# Revit family: BLAUBERG-KOMFORT_EC_S5B_270
name_source: partatom
category: Mechanical Equipment
units: mm (PartAtom-declared; Revit-internal decimal feet)

## family parameters
Always vertical = Yes
Classification = None
Cut with Voids When Loaded = No
OmniClass Number = 23.75.35.14
OmniClass Title = Air Handling Units
Part Type = Normal
Room Calculation Point = No
Round Connector Dimension = Use Diameter
Shared = No
Work Plane-Based = No

## types (4) — shared parameters
B = 300 mm
B1 = 91 mm  [stored 0.298556 ft]
B2 = 91 mm  [stored 0.298556 ft]
BHalf = 150 mm
Casing Material = Polypropylene Black
CasingR = 100 mm  [stored 0.328084 ft]
Current = 1 A
D = 125 mm  [stored 0.410105 ft]
Description = Air Handling Unit
DrainConB1 = 143 mm
DrainConB2 = 143 mm
Duct Connection Diameter = 125 mm  [stored 0.410105 ft]
ElConH = 520 mm  [stored 1.70604 ft]
ElConL = 289 mm  [stored 0.948163 ft]
Extract Air Filter = G4
Family Version = 1.0
FloorSupportH = 20 mm  [stored 0.0656168 ft]
FloorSupportHCalc = 30 mm  [stored 0.0984252 ft]
Front Maintenance Zone Height = 500 mm  [stored 1.64042 ft]
H = 844 mm  [stored 2.76903 ft]
HDuctCon = 50 mm  [stored 0.164042 ft]
Heat Exchanger Type = counter-flow
L = 578 mm  [stored 1.89633 ft]
L1 = 96 mm  [stored 0.314961 ft]
L2 = 225 mm  [stored 0.738189 ft]
L3 = 96 mm  [stored 0.314961 ft]
L4 = 225 mm  [stored 0.738189 ft]
Load Classification = HVAC
Maintenance Zone Material = Maintenance Zone
Manufacturer = Blauberg
Maximum Air Flow = 300 m³/h
Maximum Unit Power = 162 W
Metal Material = Metal Zinc
Number of Poles = 1
Plastic Material = Polypropylene Black
Power = 162 W
Power Factor = 1
RPM (min-1) = 3200
ServiceDoorH = 424 mm  [stored 1.39108 ft]
ServiceDoorH1 = 10 mm  [stored 0.0328084 ft]
ServiceDoorL = 436 mm  [stored 1.43045 ft]
ServiceDoorR = 55 mm  [stored 0.180446 ft]
ServiceDoorThickness = 5 mm  [stored 0.0164042 ft]
Sevice Door Material = Polypropylene Blue
Sound Pressure Level at 3 m (dBA) = 34
Supply Air Filter = G4 (option F8)
Transported Air Temperature (°C) = -25…+40
URL = https://blaubergventilatoren.de
Unit Current = 1 A
Voltage = 230 V
dBFloorSupports = 55 mm  [stored 0.180446 ft]
dLFloorSupports = 80 mm  [stored 0.262467 ft]

## per-type parameters (varying)
| type | Drain Connection Diameter | DrainPipe | DrainPipeD | Heat Exchanger Material | Heat recovery efficiency (%) | SEC Class | Type Comments | Weight |
| KOMFORT EC S5B 270 S21 | 15 mm  [stored 0.0492126 ft] | Yes | 15 mm  [stored 0.0492126 ft] | polystyrene | 87..98 | A+ | Air Handling Unit KOMFORT EC S5B 270 S21 | 13.00 kg |
| KOMFORT EC S5B 270-E S21 | 0 mm  [stored 0 ft] | No | 1 mm  [stored 0.00328084 ft] | enthalpy | 72..94 | A | Air Handling Unit KOMFORT EC S5B 270-E S21 | 13.50 kg |
| KOMFORT EC S5B 270 S14 | 15 mm  [stored 0.0492126 ft] | Yes | 15 mm  [stored 0.0492126 ft] | polystyrene | 87..98 | A+ | Air Handling Unit KOMFORT EC S5B 270 S14 | 13.00 kg |
| KOMFORT EC S5B 270-E S14 | 0 mm  [stored 0 ft] | No | 1 mm  [stored 0.00328084 ft] | enthalpy | 72..94 | A | Air Handling Unit KOMFORT EC S5B 270-E S14 | 13.50 kg |

note: column(s) folded — value = type name in every type: Model

note: [stored X ft] marks values corroborated as IEEE doubles in the binary element streams (Revit-internal decimal feet)

## geometry (parser evidence)
native form markers: Sweep x5
no freeform markers — native parametric forms only
